# Revit family: REVIT-TPL-SU3-2017
name_source: partatom
category: Mechanical Equipment
revit_build: Autodesk Revit 2017 (Build: 20190507_1515(x64)
units: mm (PartAtom-declared; Revit-internal decimal feet)

## family parameters
Always vertical = Yes
Cut with Voids When Loaded = No
Part Type = Normal
Room Calculation Point = No
Round Connector Dimension = Use Radius
Shared = No
Work Plane-Based = No

## types (27) — shared parameters
500-3000 GIY = 3 15/16"
A = 10"
Apparent Load = 120 VA
Assembly Code = D3040400
B = 1 5/8"
Burner Depth = 10 1/4"
Burner Height = 9 1/8"
Burner Width = 13"
Current = 5 A
Description = PVI Turbopower Low NOx - Water Heater
Disclaimer = This rendering is for building modeling purposes only. Submittal/catalog is still the contract document. PVI reserves the right to change design and specification without notice.
Drain Angle = 0.00°
Energy Radius = 14 1/2"
Flue Collector Extension = 5 1/4"
Flue Collector Radius = 11 1/4"
Flue Extension = 18 1/4"
Gas Conn X = 20 1/32"
Gas Conn Y = 13 15/16"
Gas Inlet NPT = 3/4"
Gas Inlet Radius = 3/8"
Gas Inlet X = 1/32"
Gas Inlet Y = 3 15/16"
Gas Inlet Z = 10"
Manufacturer = PVI Industries, LLC
Rear Access Extension = 0"
Relief Valve NPT = 1"
Relief Valve Radius = 1/2"
URL = www.pvi.com

## per-type parameters (varying)
- 250 L 150A-TPL: Cold Water Extension=19 1/8"; Cold Water NPT=2"; Cold Water Radius=1"; Control Panel Extension=25 1/8"; Drain Extension=22 1/8"; Drain NPT=1"; Drain Radius=1/2"; Enclosure Offset=5"; Energy Extension=23 1/8"; FC OAL=28 3/8"; Flat Side Distance=34"; Flue Diameter=4"; Flue Location=25 3/4"; Flue Radius=2"; Front Skid Extension=54 3/8"; GT Conn Z=38 3/8"; GT Z=30 3/8"; Height to Cold Inlet=15"; Height to Drain=1 7/8"; Height to Energy=26 1/2"; Height to Hot Outlet=44 7/8"; Height to Relief=51 7/8"; Hot Outlet Angle=0.00°; Hot Water Extension=19 1/8"; Hot Water NPT=2"; Hot Water Radius=1"; Input Btu/h=199000; Rear Skid Extension=18 1/8"; Recovery Rate 40F to 140F (gph)=200; Relief Extension=21 1/8"; Skid Center Dist=8 1/2"; Skid Length=36 1/4"; Skid Spacing=17"; Unit Height=63"; Unit Radius=18 1/8"; Weight=1035
- 375 L 150A-TPL: Cold Water Extension=19 1/8"; Cold Water NPT=2"; Cold Water Radius=1"; Control Panel Extension=25 1/8"; Drain Extension=22 1/8"; Drain NPT=1"; Drain Radius=1/2"; Enclosure Offset=5"; Energy Extension=23 1/8"; FC OAL=28 3/8"; Flat Side Distance=34"; Flue Diameter=4"; Flue Location=25 3/4"; Flue Radius=2"; Front Skid Extension=54 3/8"; GT Conn Z=38 3/8"; GT Z=30 3/8"; Height to Cold Inlet=15"; Height to Drain=1 7/8"; Height to Energy=26 1/2"; Height to Hot Outlet=44 7/8"; Height to Relief=51 7/8"; Hot Outlet Angle=0.00°; Hot Water Extension=19 1/8"; Hot Water NPT=2"; Hot Water Radius=1"; Input Btu/h=300000; Rear Skid Extension=18 1/8"; Recovery Rate 40F to 140F (gph)=300; Relief Extension=21 1/8"; Skid Center Dist=8 1/2"; Skid Length=36 1/4"; Skid Spacing=17"; Unit Height=63"; Unit Radius=18 1/8"; Weight=1045
- 500 L 150A-TPL: Cold Water Extension=19 1/8"; Cold Water NPT=2"; Cold Water Radius=1"; Control Panel Extension=25 1/8"; Drain Extension=22 1/8"; Drain NPT=1"; Drain Radius=1/2"; Enclosure Offset=5"; Energy Extension=23 1/8"; FC OAL=28 3/8"; Flat Side Distance=34"; Flue Diameter=5"; Flue Location=25 3/4"; Flue Radius=2 1/2"; Front Skid Extension=54 3/8"; GT Conn Z=38 3/8"; GT Z=30 3/8"; Height to Cold Inlet=15"; Height to Drain=1 7/8"; Height to Energy=26 1/2"; Height to Hot Outlet=44 7/8"; Height to Relief=51 7/8"; Hot Outlet Angle=0.00°; Hot Water Extension=19 1/8"; Hot Water NPT=2"; Hot Water Radius=1"; Input Btu/h=399000; Rear Skid Extension=18 1/8"; Recovery Rate 40F to 140F (gph)=400; Relief Extension=21 1/8"; Skid Center Dist=8 1/2"; Skid Length=36 1/4"; Skid Spacing=17"; Unit Height=63"; Unit Radius=18 1/8"; Weight=1055
- 250 L 175A-TPL: Cold Water Extension=19 1/8"; Cold Water NPT=2"; Cold Water Radius=1"; Control Panel Extension=25 1/8"; Drain Extension=22 1/8"; Drain NPT=1"; Drain Radius=1/2"; Enclosure Offset=6"; Energy Extension=23 1/8"; FC OAL=28 3/8"; Flat Side Distance=34"; Flue Diameter=4"; Flue Location=25 3/4"; Flue Radius=2"; Front Skid Extension=54 3/8"; GT Conn Z=38 3/8"; GT Z=30 3/8"; Height to Cold Inlet=15"; Height to Drain=1 7/8"; Height to Energy=26 1/2"; Height to Hot Outlet=50 7/8"; Height to Relief=57 7/8"; Hot Outlet Angle=0.00°; Hot Water Extension=19 1/8"; Hot Water NPT=2"; Hot Water Radius=1"; Input Btu/h=199000; Rear Skid Extension=18 1/8"; Recovery Rate 40F to 140F (gph)=200; Relief Extension=21 1/8"; Skid Center Dist=8 1/2"; Skid Length=36 1/4"; Skid Spacing=17"; Unit Height=69"; Unit Radius=18 1/8"; Weight=1095
- 375 L 175A-TPL: Cold Water Extension=19 1/8"; Cold Water NPT=2"; Cold Water Radius=1"; Control Panel Extension=25 1/8"; Drain Extension=22 1/8"; Drain NPT=1"; Drain Radius=1/2"; Enclosure Offset=6"; Energy Extension=23 1/8"; FC OAL=28 3/8"; Flat Side Distance=34"; Flue Diameter=4"; Flue Location=25 3/4"; Flue Radius=2"; Front Skid Extension=54 3/8"; GT Conn Z=38 3/8"; GT Z=30 3/8"; Height to Cold Inlet=15"; Height to Drain=1 7/8"; Height to Energy=26 1/2"; Height to Hot Outlet=50 7/8"; Height to Relief=57 7/8"; Hot Outlet Angle=0.00°; Hot Water Extension=19 1/8"; Hot Water NPT=2"; Hot Water Radius=1"; Input Btu/h=300000; Rear Skid Extension=18 1/8"; Recovery Rate 40F to 140F (gph)=300; Relief Extension=21 1/8"; Skid Center Dist=8 1/2"; Skid Length=36 1/4"; Skid Spacing=17"; Unit Height=69"; Unit Radius=18 1/8"; Weight=1105
- 500 L 175A-TPL: Cold Water Extension=19 1/8"; Cold Water NPT=2"; Cold Water Radius=1"; Control Panel Extension=25 1/8"; Drain Extension=22 1/8"; Drain NPT=1"; Drain Radius=1/2"; Enclosure Offset=6"; Energy Extension=23 1/8"; FC OAL=28 3/8"; Flat Side Distance=34"; Flue Diameter=5"; Flue Location=25 3/4"; Flue Radius=2 1/2"; Front Skid Extension=54 3/8"; GT Conn Z=38 3/8"; GT Z=30 3/8"; Height to Cold Inlet=15"; Height to Drain=1 7/8"; Height to Energy=26 1/2"; Height to Hot Outlet=50 7/8"; Height to Relief=57 7/8"; Hot Outlet Angle=0.00°; Hot Water Extension=19 1/8"; Hot Water NPT=2"; Hot Water Radius=1"; Input Btu/h=399000; Rear Skid Extension=18 1/8"; Recovery Rate 40F to 140F (gph)=400; Relief Extension=21 1/8"; Skid Center Dist=8 1/2"; Skid Length=36 1/4"; Skid Spacing=17"; Unit Height=69"; Unit Radius=18 1/8"; Weight=1115
- 250 L 215A-TPL: Cold Water Extension=19 1/8"; Cold Water NPT=2"; Cold Water Radius=1"; Control Panel Extension=25 1/8"; Drain Extension=22 1/8"; Drain NPT=1"; Drain Radius=1/2"; Enclosure Offset=6"; Energy Extension=23 1/8"; FC OAL=28 3/8"; Flat Side Distance=34"; Flue Diameter=4"; Flue Location=25 3/4"; Flue Radius=2"; Front Skid Extension=54 3/8"; GT Conn Z=38 3/8"; GT Z=30 3/8"; Height to Cold Inlet=15"; Height to Drain=1 7/8"; Height to Energy=26 1/2"; Height to Hot Outlet=64 1/4"; Height to Relief=64 7/8"; Hot Outlet Angle=90.00°; Hot Water Extension=19 1/8"; Hot Water NPT=2"; Hot Water Radius=1"; Input Btu/h=199000; Rear Skid Extension=18 1/8"; Recovery Rate 40F to 140F (gph)=200; Relief Extension=21 1/8"; Skid Center Dist=8 1/2"; Skid Length=36 1/4"; Skid Spacing=17"; Unit Height=76"; Unit Radius=18 1/8"; Weight=1135
- 375 L 215A-TPL: Cold Water Extension=19 1/8"; Cold Water NPT=2"; Cold Water Radius=1"; Control Panel Extension=25 1/8"; Drain Extension=22 1/8"; Drain NPT=1"; Drain Radius=1/2"; Enclosure Offset=6"; Energy Extension=23 1/8"; FC OAL=28 3/8"; Flat Side Distance=34"; Flue Diameter=4"; Flue Location=25 3/4"; Flue Radius=2"; Front Skid Extension=54 3/8"; GT Conn Z=38 3/8"; GT Z=30 3/8"; Height to Cold Inlet=15"; Height to Drain=1 7/8"; Height to Energy=26 1/2"; Height to Hot Outlet=64 1/4"; Height to Relief=64 7/8"; Hot Outlet Angle=90.00°; Hot Water Extension=19 1/8"; Hot Water NPT=2"; Hot Water Radius=1"; Input Btu/h=300000; Rear Skid Extension=18 1/8"; Recovery Rate 40F to 140F (gph)=300; Relief Extension=21 1/8"; Skid Center Dist=8 1/2"; Skid Length=36 1/4"; Skid Spacing=17"; Unit Height=76"; Unit Radius=18 1/8"; Weight=1145
- 500 L 215A-TPL: Cold Water Extension=19 1/8"; Cold Water NPT=2"; Cold Water Radius=1"; Control Panel Extension=25 1/8"; Drain Extension=22 1/8"; Drain NPT=1"; Drain Radius=1/2"; Enclosure Offset=6"; Energy Extension=23 1/8"; FC OAL=28 3/8"; Flat Side Distance=34"; Flue Diameter=5"; Flue Location=25 3/4"; Flue Radius=2 1/2"; Front Skid Extension=54 3/8"; GT Conn Z=38 3/8"; GT Z=30 3/8"; Height to Cold Inlet=15"; Height to Drain=1 7/8"; Height to Energy=26 1/2"; Height to Hot Outlet=64 1/4"; Height to Relief=64 7/8"; Hot Outlet Angle=90.00°; Hot Water Extension=19 1/8"; Hot Water NPT=2"; Hot Water Radius=1"; Input Btu/h=399000; Rear Skid Extension=18 1/8"; Recovery Rate 40F to 140F (gph)=400; Relief Extension=21 1/8"; Skid Center Dist=8 1/2"; Skid Length=36 1/4"; Skid Spacing=17"; Unit Height=76"; Unit Radius=18 1/8"; Weight=1155
- 250 L 250A-TPL: Cold Water Extension=23 5/8"; Cold Water NPT=2"; Cold Water Radius=1"; Control Panel Extension=29 5/8"; Drain Extension=26 5/8"; Drain NPT=1"; Drain Radius=1/2"; Enclosure Offset=4"; Energy Extension=27 1/8"; FC OAL=32 3/8"; Flat Side Distance=45 1/4"; Flue Diameter=4"; Flue Location=29 3/4"; Flue Radius=2"; Front Skid Extension=68 1/8"; GT Conn Z=42 3/8"; GT Z=34 3/8"; Height to Cold Inlet=17 1/16"; Height to Drain=1 7/8"; Height to Energy=28 3/4"; Height to Hot Outlet=44 7/8"; Height to Relief=54 1/8"; Hot Outlet Angle=0.00°; Hot Water Extension=23 5/8"; Hot Water NPT=2"; Hot Water Radius=1"; Input Btu/h=199000; Rear Skid Extension=22 5/8"; Recovery Rate 40F to 140F (gph)=200; Relief Extension=25 5/8"; Skid Center Dist=13 1/2"; Skid Length=45 1/2"; Skid Spacing=27"; Unit Height=67 1/2"; Unit Radius=22 5/8"; Weight=1330
- 375 L 250A-TPL: Cold Water Extension=23 5/8"; Cold Water NPT=2"; Cold Water Radius=1"; Control Panel Extension=29 5/8"; Drain Extension=26 5/8"; Drain NPT=1"; Drain Radius=1/2"; Enclosure Offset=4"; Energy Extension=27 1/8"; FC OAL=32 3/8"; Flat Side Distance=45 1/4"; Flue Diameter=4"; Flue Location=29 3/4"; Flue Radius=2"; Front Skid Extension=68 1/8"; GT Conn Z=42 3/8"; GT Z=34 3/8"; Height to Cold Inlet=17 1/16"; Height to Drain=1 7/8"; Height to Energy=28 3/4"; Height to Hot Outlet=44 7/8"; Height to Relief=54 1/8"; Hot Outlet Angle=0.00°; Hot Water Extension=23 5/8"; Hot Water NPT=2"; Hot Water Radius=1"; Input Btu/h=300000; Rear Skid Extension=22 5/8"; Recovery Rate 40F to 140F (gph)=300; Relief Extension=25 5/8"; Skid Center Dist=13 1/2"; Skid Length=45 1/2"; Skid Spacing=27"; Unit Height=67 1/2"; Unit Radius=22 5/8"; Weight=1340
- 500 L 250A-TPL: Cold Water Extension=23 5/8"; Cold Water NPT=2"; Cold Water Radius=1"; Control Panel Extension=29 5/8"; Drain Extension=26 5/8"; Drain NPT=1"; Drain Radius=1/2"; Enclosure Offset=4"; Energy Extension=27 1/8"; FC OAL=32 3/8"; Flat Side Distance=45 1/4"; Flue Diameter=5"; Flue Location=29 3/4"; Flue Radius=2 1/2"; Front Skid Extension=68 1/8"; GT Conn Z=42 3/8"; GT Z=34 3/8"; Height to Cold Inlet=17 1/16"; Height to Drain=1 7/8"; Height to Energy=28 3/4"; Height to Hot Outlet=44 7/8"; Height to Relief=54 1/8"; Hot Outlet Angle=0.00°; Hot Water Extension=23 5/8"; Hot Water NPT=2"; Hot Water Radius=1"; Input Btu/h=399000; Rear Skid Extension=22 5/8"; Recovery Rate 40F to 140F (gph)=400; Relief Extension=25 5/8"; Skid Center Dist=13 1/2"; Skid Length=45 1/2"; Skid Spacing=27"; Unit Height=67 1/2"; Unit Radius=22 5/8"; Weight=1350
- 250 L 300A-TPL: Cold Water Extension=23 5/8"; Cold Water NPT=2"; Cold Water Radius=1"; Control Panel Extension=29 5/8"; Drain Extension=26 5/8"; Drain NPT=1"; Drain Radius=1/2"; Enclosure Offset=5"; Energy Extension=27 1/8"; FC OAL=32 3/8"; Flat Side Distance=45 1/4"; Flue Diameter=4"; Flue Location=29 3/4"; Flue Radius=2"; Front Skid Extension=68 1/8"; GT Conn Z=42 3/8"; GT Z=34 3/8"; Height to Cold Inlet=17 1/16"; Height to Drain=1 7/8"; Height to Energy=28 3/4"; Height to Hot Outlet=50 7/8"; Height to Relief=57 1/8"; Hot Outlet Angle=0.00°; Hot Water Extension=23 5/8"; Hot Water NPT=2"; Hot Water Radius=1"; Input Btu/h=199000; Rear Skid Extension=22 5/8"; Recovery Rate 40F to 140F (gph)=200; Relief Extension=25 5/8"; Skid Center Dist=13 1/2"; Skid Length=45 1/2"; Skid Spacing=27"; Unit Height=73 1/2"; Unit Radius=22 5/8"; Weight=1390
- 375 L 300A-TPL: Cold Water Extension=23 5/8"; Cold Water NPT=2"; Cold Water Radius=1"; Control Panel Extension=29 5/8"; Drain Extension=26 5/8"; Drain NPT=1"; Drain Radius=1/2"; Enclosure Offset=5"; Energy Extension=27 1/8"; FC OAL=32 3/8"; Flat Side Distance=45 1/4"; Flue Diameter=4"; Flue Location=29 3/4"; Flue Radius=2"; Front Skid Extension=68 1/8"; GT Conn Z=42 3/8"; GT Z=34 3/8"; Height to Cold Inlet=17 1/16"; Height to Drain=1 7/8"; Height to Energy=28 3/4"; Height to Hot Outlet=50 7/8"; Height to Relief=57 1/8"; Hot Outlet Angle=0.00°; Hot Water Extension=23 5/8"; Hot Water NPT=2"; Hot Water Radius=1"; Input Btu/h=300000; Rear Skid Extension=22 5/8"; Recovery Rate 40F to 140F (gph)=300; Relief Extension=25 5/8"; Skid Center Dist=13 1/2"; Skid Length=45 1/2"; Skid Spacing=27"; Unit Height=73 1/2"; Unit Radius=22 5/8"; Weight=1400
- 500 L 300A-TPL: Cold Water Extension=23 5/8"; Cold Water NPT=2"; Cold Water Radius=1"; Control Panel Extension=29 5/8"; Drain Extension=26 5/8"; Drain NPT=1"; Drain Radius=1/2"; Enclosure Offset=5"; Energy Extension=27 1/8"; FC OAL=32 3/8"; Flat Side Distance=45 1/4"; Flue Diameter=5"; Flue Location=29 3/4"; Flue Radius=2 1/2"; Front Skid Extension=68 1/8"; GT Conn Z=42 3/8"; GT Z=34 3/8"; Height to Cold Inlet=17 1/16"; Height to Drain=1 7/8"; Height to Energy=28 3/4"; Height to Hot Outlet=50 7/8"; Height to Relief=57 1/8"; Hot Outlet Angle=0.00°; Hot Water Extension=23 5/8"; Hot Water NPT=2"; Hot Water Radius=1"; Input Btu/h=399000; Rear Skid Extension=22 5/8"; Recovery Rate 40F to 140F (gph)=400; Relief Extension=25 5/8"; Skid Center Dist=13 1/2"; Skid Length=45 1/2"; Skid Spacing=27"; Unit Height=73 1/2"; Unit Radius=22 5/8"; Weight=1410
- 250 L 400A-TPL: Cold Water Extension=23 5/8"; Cold Water NPT=2"; Cold Water Radius=1"; Control Panel Extension=29 5/8"; Drain Extension=26 5/8"; Drain NPT=1"; Drain Radius=1/2"; Enclosure Offset=16 1/2"; Energy Extension=27 1/8"; FC OAL=32 3/8"; Flat Side Distance=45 1/4"; Flue Diameter=4"; Flue Location=29 3/4"; Flue Radius=2"; Front Skid Extension=68 1/8"; GT Conn Z=42 3/8"; GT Z=34 3/8"; Height to Cold Inlet=17 1/16"; Height to Drain=1 7/8"; Height to Energy=28 3/4"; Height to Hot Outlet=68 1/2"; Height to Relief=69 1/8"; Hot Outlet Angle=90.00°; Hot Water Extension=23 5/8"; Hot Water NPT=2"; Hot Water Radius=1"; Input Btu/h=199000; Rear Skid Extension=22 5/8"; Recovery Rate 40F to 140F (gph)=200; Relief Extension=25 5/8"; Skid Center Dist=13 1/2"; Skid Length=45 1/2"; Skid Spacing=27"; Unit Height=85 1/2"; Unit Radius=22 5/8"; Weight=1435
- 375 L 400A-TPL: Cold Water Extension=23 5/8"; Cold Water NPT=2"; Cold Water Radius=1"; Control Panel Extension=29 5/8"; Drain Extension=26 5/8"; Drain NPT=1"; Drain Radius=1/2"; Enclosure Offset=16 1/2"; Energy Extension=27 1/8"; FC OAL=32 3/8"; Flat Side Distance=45 1/4"; Flue Diameter=4"; Flue Location=29 3/4"; Flue Radius=2"; Front Skid Extension=68 1/8"; GT Conn Z=42 3/8"; GT Z=34 3/8"; Height to Cold Inlet=17 1/16"; Height to Drain=1 7/8"; Height to Energy=28 3/4"; Height to Hot Outlet=68 1/2"; Height to Relief=69 1/8"; Hot Outlet Angle=90.00°; Hot Water Extension=23 5/8"; Hot Water NPT=2"; Hot Water Radius=1"; Input Btu/h=300000; Rear Skid Extension=22 5/8"; Recovery Rate 40F to 140F (gph)=300; Relief Extension=25 5/8"; Skid Center Dist=13 1/2"; Skid Length=45 1/2"; Skid Spacing=27"; Unit Height=85 1/2"; Unit Radius=22 5/8"; Weight=1445
- 500 L 400A-TPL: Cold Water Extension=23 5/8"; Cold Water NPT=2"; Cold Water Radius=1"; Control Panel Extension=29 5/8"; Drain Extension=26 5/8"; Drain NPT=1"; Drain Radius=1/2"; Enclosure Offset=16 1/2"; Energy Extension=27 1/8"; FC OAL=32 3/8"; Flat Side Distance=45 1/4"; Flue Diameter=5"; Flue Location=29 3/4"; Flue Radius=2 1/2"; Front Skid Extension=68 1/8"; GT Conn Z=42 3/8"; GT Z=34 3/8"; Height to Cold Inlet=17 1/16"; Height to Drain=1 7/8"; Height to Energy=28 3/4"; Height to Hot Outlet=68 1/2"; Height to Relief=69 1/8"; Hot Outlet Angle=90.00°; Hot Water Extension=23 5/8"; Hot Water NPT=2"; Hot Water Radius=1"; Input Btu/h=399000; Rear Skid Extension=22 5/8"; Recovery Rate 40F to 140F (gph)=400; Relief Extension=25 5/8"; Skid Center Dist=13 1/2"; Skid Length=45 1/2"; Skid Spacing=27"; Unit Height=85 1/2"; Unit Radius=22 5/8"; Weight=1455
- 250 L 500A-TPL: Cold Water Extension=28 7/8"; Cold Water NPT=3"; Cold Water Radius=1 1/2"; Control Panel Extension=34 7/8"; Drain Extension=31 7/8"; Drain NPT=1 1/2"; Drain Radius=3/4"; Enclosure Offset=7 1/2"; Energy Extension=32 5/8"; FC OAL=37 7/8"; Flat Side Distance=55 3/4"; Flue Diameter=4"; Flue Location=35 1/4"; Flue Radius=2"; Front Skid Extension=82 7/8"; GT Conn Z=47 7/8"; GT Z=39 7/8"; Height to Cold Inlet=18 1/4"; Height to Drain=2 1/4"; Height to Energy=30"; Height to Hot Outlet=57 3/8"; Height to Relief=58"; Hot Outlet Angle=90.00°; Hot Water Extension=28 7/8"; Hot Water NPT=3"; Hot Water Radius=1 1/2"; Input Btu/h=199000; Rear Skid Extension=27 7/8"; Recovery Rate 40F to 140F (gph)=200; Relief Extension=30 7/8"; Skid Center Dist=13 1/2"; Skid Length=55"; Skid Spacing=27"; Unit Height=75 3/4"; Unit Radius=27 7/8"; Weight=1815
- 375 L 500A-TPL: Cold Water Extension=28 7/8"; Cold Water NPT=3"; Cold Water Radius=1 1/2"; Control Panel Extension=34 7/8"; Drain Extension=31 7/8"; Drain NPT=1 1/2"; Drain Radius=3/4"; Enclosure Offset=7 1/2"; Energy Extension=32 5/8"; FC OAL=37 7/8"; Flat Side Distance=55 3/4"; Flue Diameter=4"; Flue Location=35 1/4"; Flue Radius=2"; Front Skid Extension=82 7/8"; GT Conn Z=47 7/8"; GT Z=39 7/8"; Height to Cold Inlet=18 1/4"; Height to Drain=2 1/4"; Height to Energy=30"; Height to Hot Outlet=57 3/8"; Height to Relief=58"; Hot Outlet Angle=90.00°; Hot Water Extension=28 7/8"; Hot Water NPT=3"; Hot Water Radius=1 1/2"; Input Btu/h=300000; Rear Skid Extension=27 7/8"; Recovery Rate 40F to 140F (gph)=300; Relief Extension=30 7/8"; Skid Center Dist=13 1/2"; Skid Length=55"; Skid Spacing=27"; Unit Height=75 3/4"; Unit Radius=27 7/8"; Weight=1825
- 500 L 500A-TPL: Cold Water Extension=28 7/8"; Cold Water NPT=3"; Cold Water Radius=1 1/2"; Control Panel Extension=34 7/8"; Drain Extension=31 7/8"; Drain NPT=1 1/2"; Drain Radius=3/4"; Enclosure Offset=7 1/2"; Energy Extension=32 5/8"; FC OAL=37 7/8"; Flat Side Distance=55 3/4"; Flue Diameter=5"; Flue Location=35 1/4"; Flue Radius=2 1/2"; Front Skid Extension=82 7/8"; GT Conn Z=47 7/8"; GT Z=39 7/8"; Height to Cold Inlet=18 1/4"; Height to Drain=2 1/4"; Height to Energy=30"; Height to Hot Outlet=57 3/8"; Height to Relief=58"; Hot Outlet Angle=90.00°; Hot Water Extension=28 7/8"; Hot Water NPT=3"; Hot Water Radius=1 1/2"; Input Btu/h=399000; Rear Skid Extension=27 7/8"; Recovery Rate 40F to 140F (gph)=400; Relief Extension=30 7/8"; Skid Center Dist=13 1/2"; Skid Length=55"; Skid Spacing=27"; Unit Height=75 3/4"; Unit Radius=27 7/8"; Weight=1835
- 250 L 600A-TPL: Cold Water Extension=28 7/8"; Cold Water NPT=3"; Cold Water Radius=1 1/2"; Control Panel Extension=34 7/8"; Drain Extension=31 7/8"; Drain NPT=1 1/2"; Drain Radius=3/4"; Enclosure Offset=19 5/8"; Energy Extension=32 5/8"; FC OAL=37 7/8"; Flat Side Distance=55 3/4"; Flue Diameter=4"; Flue Location=35 1/4"; Flue Radius=2"; Front Skid Extension=82 7/8"; GT Conn Z=47 7/8"; GT Z=39 7/8"; Height to Cold Inlet=18 1/4"; Height to Drain=2 1/4"; Height to Energy=30"; Height to Hot Outlet=69 3/8"; Height to Relief=70"; Hot Outlet Angle=90.00°; Hot Water Extension=28 7/8"; Hot Water NPT=3"; Hot Water Radius=1 1/2"; Input Btu/h=199000; Rear Skid Extension=27 7/8"; Recovery Rate 40F to 140F (gph)=200; Relief Extension=30 7/8"; Skid Center Dist=13 1/2"; Skid Length=55"; Skid Spacing=27"; Unit Height=87 3/4"; Unit Radius=27 7/8"; Weight=2040
- 375 L 600A-TPL: Cold Water Extension=28 7/8"; Cold Water NPT=3"; Cold Water Radius=1 1/2"; Control Panel Extension=34 7/8"; Drain Extension=31 7/8"; Drain NPT=1 1/2"; Drain Radius=3/4"; Enclosure Offset=19 5/8"; Energy Extension=32 5/8"; FC OAL=37 7/8"; Flat Side Distance=55 3/4"; Flue Diameter=4"; Flue Location=35 1/4"; Flue Radius=2"; Front Skid Extension=82 7/8"; GT Conn Z=47 7/8"; GT Z=39 7/8"; Height to Cold Inlet=18 1/4"; Height to Drain=2 1/4"; Height to Energy=30"; Height to Hot Outlet=69 3/8"; Height to Relief=70"; Hot Outlet Angle=90.00°; Hot Water Extension=28 7/8"; Hot Water NPT=3"; Hot Water Radius=1 1/2"; Input Btu/h=300000; Rear Skid Extension=27 7/8"; Recovery Rate 40F to 140F (gph)=300; Relief Extension=30 7/8"; Skid Center Dist=13 1/2"; Skid Length=55"; Skid Spacing=27"; Unit Height=87 3/4"; Unit Radius=27 7/8"; Weight=2050
- 500 L 600A-TPL: Cold Water Extension=28 7/8"; Cold Water NPT=3"; Cold Water Radius=1 1/2"; Control Panel Extension=34 7/8"; Drain Extension=31 7/8"; Drain NPT=1 1/2"; Drain Radius=3/4"; Enclosure Offset=19 5/8"; Energy Extension=32 5/8"; FC OAL=37 7/8"; Flat Side Distance=55 3/4"; Flue Diameter=5"; Flue Location=35 1/4"; Flue Radius=2 1/2"; Front Skid Extension=82 7/8"; GT Conn Z=47 7/8"; GT Z=39 7/8"; Height to Cold Inlet=18 1/4"; Height to Drain=2 1/4"; Height to Energy=30"; Height to Hot Outlet=69 3/8"; Height to Relief=70"; Hot Outlet Angle=90.00°; Hot Water Extension=28 7/8"; Hot Water NPT=3"; Hot Water Radius=1 1/2"; Input Btu/h=399000; Rear Skid Extension=27 7/8"; Recovery Rate 40F to 140F (gph)=400; Relief Extension=30 7/8"; Skid Center Dist=13 1/2"; Skid Length=55"; Skid Spacing=27"; Unit Height=87 3/4"; Unit Radius=27 7/8"; Weight=2060
- 250 L 750A-TPL: Cold Water Extension=34 1/4"; Cold Water NPT=3"; Cold Water Radius=1 1/2"; Control Panel Extension=40 1/4"; Drain Extension=37 1/4"; Drain NPT=1 1/2"; Drain Radius=3/4"; Enclosure Offset=12"; Energy Extension=38 1/4"; FC OAL=43 1/2"; Flat Side Distance=66 1/2"; Flue Diameter=4"; Flue Location=40 7/8"; Flue Radius=2"; Front Skid Extension=100 1/4"; GT Conn Z=53 1/2"; GT Z=45 1/2"; Height to Cold Inlet=21 1/4"; Height to Drain=2 1/4"; Height to Energy=32 5/8"; Height to Hot Outlet=60 7/8"; Height to Relief=61 1/2"; Hot Outlet Angle=90.00°; Hot Water Extension=34 1/4"; Hot Water NPT=3"; Hot Water Radius=1 1/2"; Input Btu/h=199000; Rear Skid Extension=33 1/4"; Recovery Rate 40F to 140F (gph)=200; Relief Extension=36 1/4"; Skid Center Dist=18"; Skid Length=67"; Skid Spacing=36"; Unit Height=81 1/4"; Unit Radius=33 1/4"; Weight=2780
- 375 L 750A-TPL: Cold Water Extension=34 1/4"; Cold Water NPT=3"; Cold Water Radius=1 1/2"; Control Panel Extension=40 1/4"; Drain Extension=37 1/4"; Drain NPT=1 1/2"; Drain Radius=3/4"; Enclosure Offset=12"; Energy Extension=38 1/4"; FC OAL=43 1/2"; Flat Side Distance=66 1/2"; Flue Diameter=4"; Flue Location=40 7/8"; Flue Radius=2"; Front Skid Extension=100 1/4"; GT Conn Z=53 1/2"; GT Z=45 1/2"; Height to Cold Inlet=21 1/4"; Height to Drain=2 1/4"; Height to Energy=32 5/8"; Height to Hot Outlet=60 7/8"; Height to Relief=61 1/2"; Hot Outlet Angle=90.00°; Hot Water Extension=34 1/4"; Hot Water NPT=3"; Hot Water Radius=1 1/2"; Input Btu/h=300000; Rear Skid Extension=33 1/4"; Recovery Rate 40F to 140F (gph)=300; Relief Extension=36 1/4"; Skid Center Dist=18"; Skid Length=67"; Skid Spacing=36"; Unit Height=81 1/4"; Unit Radius=33 1/4"; Weight=2780
- 500 L 750A-TPL: Cold Water Extension=34 1/4"; Cold Water NPT=3"; Cold Water Radius=1 1/2"; Control Panel Extension=40 1/4"; Drain Extension=37 1/4"; Drain NPT=1 1/2"; Drain Radius=3/4"; Enclosure Offset=12"; Energy Extension=38 1/4"; FC OAL=43 1/2"; Flat Side Distance=66 1/2"; Flue Diameter=5"; Flue Location=40 7/8"; Flue Radius=2 1/2"; Front Skid Extension=100 1/4"; GT Conn Z=53 1/2"; GT Z=45 1/2"; Height to Cold Inlet=21 1/4"; Height to Drain=2 1/4"; Height to Energy=32 5/8"; Height to Hot Outlet=60 7/8"; Height to Relief=61 1/2"; Hot Outlet Angle=90.00°; Hot Water Extension=34 1/4"; Hot Water NPT=3"; Hot Water Radius=1 1/2"; Input Btu/h=399000; Rear Skid Extension=33 1/4"; Recovery Rate 40F to 140F (gph)=400; Relief Extension=36 1/4"; Skid Center Dist=18"; Skid Length=67"; Skid Spacing=36"; Unit Height=81 1/4"; Unit Radius=33 1/4"; Weight=2780

note: column(s) folded — value = type name in every type: Model

## geometry (parser evidence)
native form markers: Blend x2, Sweep x3
no freeform markers — native parametric forms only
